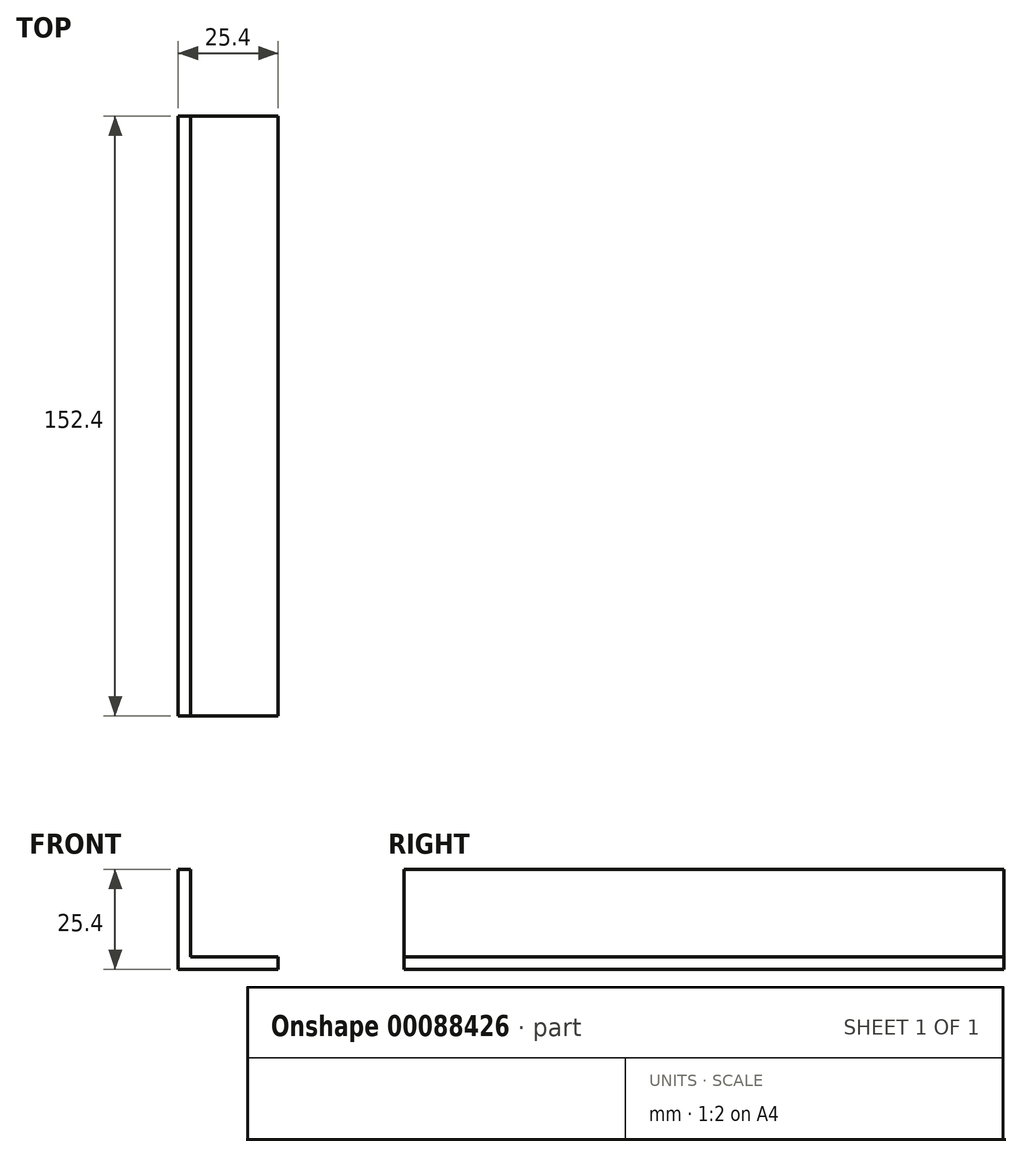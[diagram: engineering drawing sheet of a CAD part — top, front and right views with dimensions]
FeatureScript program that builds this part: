
annotation { "Feature Type Name" : "Feature", "Feature Type Description" : "" }
export const myFeature = defineFeature(function(context is Context, id is Id, definition is map)
    precondition{}
    {
        {
            var Q0;
            Q0=qCreatedBy(makeId("Front.planeOp"),FACE);
            var sketch = newSketch(context, id + "F0", { "sketchPlane" : qUnion([Q0])});
            skLineSegment(sketch, "E0", {"start": v(0, 0) * mm, "end": v(0, 25.4) * mm});
            skLineSegment(sketch, "E1", {"start": v(0, 25.4) * mm, "end": v(3.18, 25.4) * mm});
            skLineSegment(sketch, "E2", {"start": v(3.18, 25.4) * mm, "end": v(3.18, 3.17) * mm});
            skLineSegment(sketch, "E3", {"start": v(3.18, 3.17) * mm, "end": v(25.4, 3.18) * mm});
            skLineSegment(sketch, "E4", {"start": v(25.4, 3.18) * mm, "end": v(25.4, 0) * mm});
            skLineSegment(sketch, "E5", {"start": v(25.4, 0) * mm, "end": v(0, 0) * mm});
            skSolve(sketch);
        }
        {
            var Q0;
            Q0=makeQuery(id+"F0.imprint","IMPRINT",FACE,{"disambiguationData":[TD([[makeQuery(id+"F0.imprint","IMPRINT",EDGE,{"derivedFrom":sQuery(id+"F0.wireOp",EDGE,"E0")}),-1.0]])]});
            extrude(context, id + "F1", {"entities" : qUnion([Q0]), "depth" : 152.4 * mm});
        }
    });
